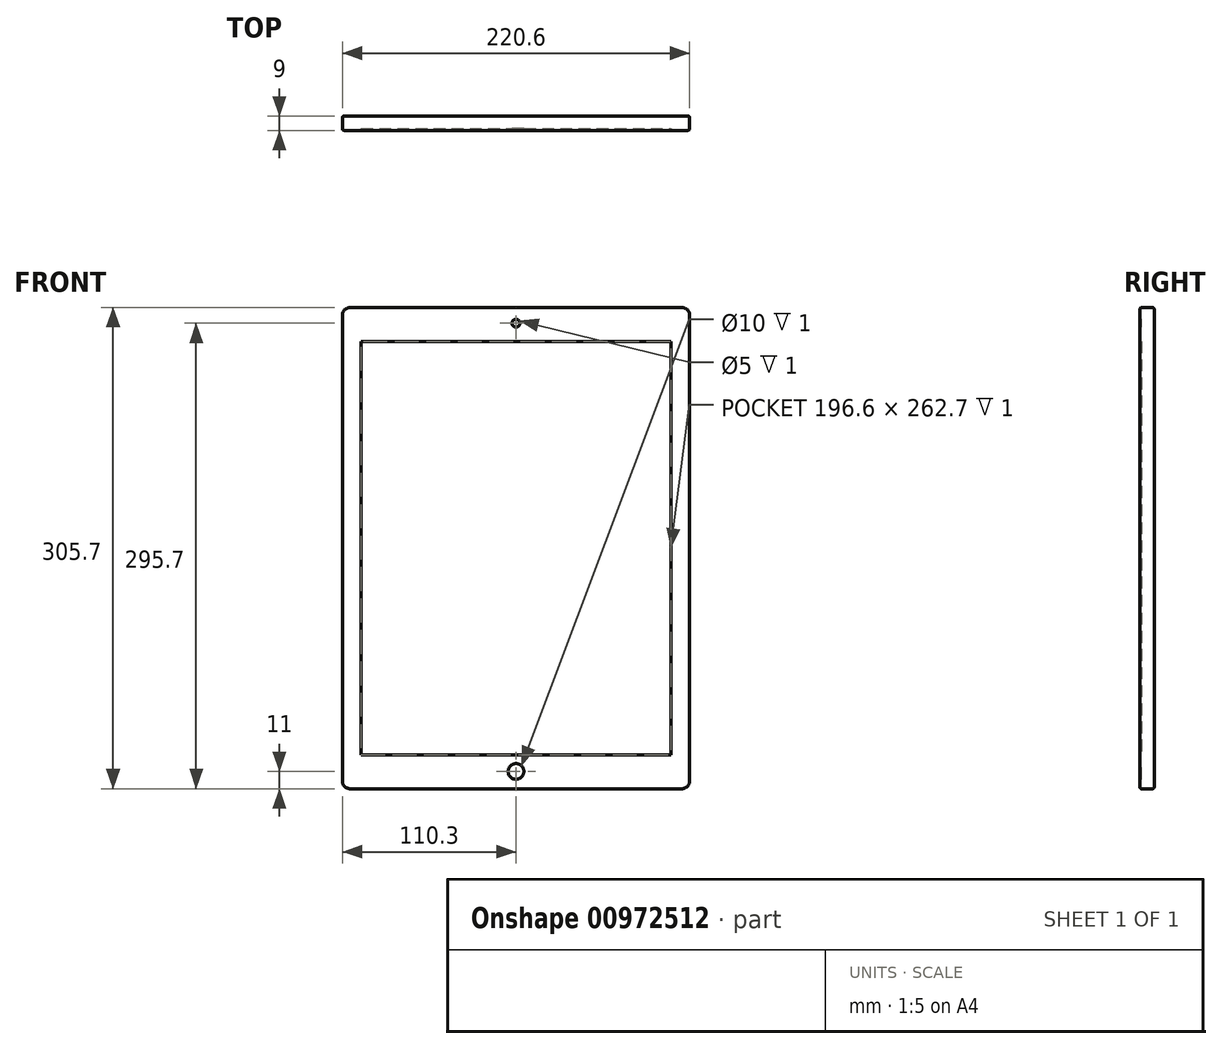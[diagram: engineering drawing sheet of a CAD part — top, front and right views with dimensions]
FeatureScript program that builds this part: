
annotation { "Feature Type Name" : "Feature", "Feature Type Description" : "" }
export const myFeature = defineFeature(function(context is Context, id is Id, definition is map)
    precondition{}
    {
        {
            var Q0;
            Q0=qCreatedBy(makeId("Front.planeOp"),FACE);
            var sketch = newSketch(context, id + "F0", { "sketchPlane" : qUnion([Q0])});
            skLineSegment(sketch, "E0.bottom", {"start": v(-110.3, 305.7) * mm, "end": v(110.3, 305.7) * mm});
            skLineSegment(sketch, "E0.top", {"start": v(-110.3, 0) * mm, "end": v(110.3, 0) * mm});
            skLineSegment(sketch, "E0.left", {"start": v(-110.3, 305.7) * mm, "end": v(-110.3, 0) * mm});
            skLineSegment(sketch, "E0.right", {"start": v(110.3, 305.7) * mm, "end": v(110.3, 0) * mm});
            skSolve(sketch);
        }
        {
            var Q0;
            Q0=makeQuery(id+"F0.imprint","IMPRINT",FACE,{"disambiguationData":[TD([[makeQuery(id+"F0.imprint","IMPRINT",EDGE,{"derivedFrom":sQuery(id+"F0.wireOp",EDGE,"E0.bottom")}),-1.0]])]});
            extrude(context, id + "F1", {"entities" : qUnion([Q0]), "depth" : 9 * mm, "offsetDistance" : 25 * mm});
        }
        {
            var Q0;
            Q0=makeQuery(id+"F1.opExtrude","CAP_FACE",FACE,{"disambiguationData":[OSD([sQuery(id+"F0.wireOp",EDGE,"E0.bottom"),sQuery(id+"F0.wireOp",EDGE,"E0.top"),sQuery(id+"F0.wireOp",EDGE,"E0.left"),sQuery(id+"F0.wireOp",EDGE,"E0.right")])],"isStart":false});
            var sketch = newSketch(context, id + "F2", { "sketchPlane" : qUnion([Q0])});
            skLineSegment(sketch, "E1.bottom", {"start": v(-98.3, 284.2) * mm, "end": v(98.3, 284.2) * mm});
            skLineSegment(sketch, "E1.top", {"start": v(-98.3, 21.5) * mm, "end": v(98.3, 21.5) * mm});
            skLineSegment(sketch, "E1.left", {"start": v(-98.3, 284.2) * mm, "end": v(-98.3, 21.5) * mm});
            skLineSegment(sketch, "E1.right", {"start": v(98.3, 284.2) * mm, "end": v(98.3, 21.5) * mm});
            skLineSegment(sketch, "E2", {"start": v(0, 0) * mm, "end": v(0, 21.5) * mm, "construction": true});
            skLineSegment(sketch, "E3", {"start": v(0, 305.7) * mm, "end": v(0, 284.2) * mm, "construction": true});
            skSolve(sketch);
        }
        {
            var Q0;
            Q0=makeQuery(id+"F2.imprint","IMPRINT",FACE,{"disambiguationData":[TD([[makeQuery(id+"F2.imprint","IMPRINT",EDGE,{"derivedFrom":sQuery(id+"F2.wireOp",EDGE,"E1.bottom")}),-1.0]])]});
            extrude(context, id + "F3", {"entities" : qUnion([Q0]), "operationType" : NewBodyOperationType.REMOVE, "oppositeDirection" : true, "depth" : 1 * mm, "offsetDistance" : 25 * mm});
        }
        {
            var Q0;
            Q0=makeQuery(id+"F1.opExtrude","CAP_FACE",FACE,{"disambiguationData":[OSD([sQuery(id+"F0.wireOp",EDGE,"E0.bottom"),sQuery(id+"F0.wireOp",EDGE,"E0.top"),sQuery(id+"F0.wireOp",EDGE,"E0.left"),sQuery(id+"F0.wireOp",EDGE,"E0.right")])],"isStart":false});
            var sketch = newSketch(context, id + "F4", { "sketchPlane" : qUnion([Q0])});
            skCircle(sketch, "E4", {"center": v(0, 295.7) * mm, "radius": 2.5 * mm});
            skCircle(sketch, "E5", {"center": v(0, 11) * mm, "radius": 5 * mm});
            skLineSegment(sketch, "E6", {"start": v(0, 295.7) * mm, "end": v(0, 11) * mm, "construction": true});
            skLineSegment(sketch, "E7", {"start": v(0, 0) * mm, "end": v(0, 11) * mm, "construction": true});
            skSolve(sketch);
        }
        {
            var Q0;
            Q0=makeQuery(id+"F4.imprint","IMPRINT",FACE,{"disambiguationData":[TD([[makeQuery(id+"F4.imprint","IMPRINT",EDGE,{"derivedFrom":sQuery(id+"F4.wireOp",EDGE,"E4")}),1.0]])]});
            var Q1;
            Q1=makeQuery(id+"F4.imprint","IMPRINT",FACE,{"disambiguationData":[TD([[makeQuery(id+"F4.imprint","IMPRINT",EDGE,{"derivedFrom":sQuery(id+"F4.wireOp",EDGE,"E5")}),1.0]])]});
            extrude(context, id + "F5", {"entities" : qUnion([Q0, Q1]), "operationType" : NewBodyOperationType.REMOVE, "oppositeDirection" : true, "depth" : 1 * mm, "offsetDistance" : 25 * mm});
        }
        {
            var Q0;
            Q0=makeQuery(id+"F1.opExtrude","SWEPT_EDGE",EDGE,{"disambiguationData":[OSD([sQuery(id+"F0.wireOp",EDGE,"E0.top"),sQuery(id+"F0.wireOp",EDGE,"E0.left")])]});
            var Q1;
            Q1=makeQuery(id+"F1.opExtrude","SWEPT_EDGE",EDGE,{"disambiguationData":[OSD([sQuery(id+"F0.wireOp",EDGE,"E0.top"),sQuery(id+"F0.wireOp",EDGE,"E0.right")])]});
            var Q2;
            Q2=makeQuery(id+"F1.opExtrude","SWEPT_EDGE",EDGE,{"disambiguationData":[OSD([sQuery(id+"F0.wireOp",EDGE,"E0.bottom"),sQuery(id+"F0.wireOp",EDGE,"E0.right")])]});
            var Q3;
            Q3=makeQuery(id+"F1.opExtrude","SWEPT_EDGE",EDGE,{"disambiguationData":[OSD([sQuery(id+"F0.wireOp",EDGE,"E0.bottom"),sQuery(id+"F0.wireOp",EDGE,"E0.left")])]});
            fillet(context, id + "F6", {"entities" : qUnion([Q0, Q1, Q2, Q3]), "radius" : 5 * mm, "tangentPropagation" : true, "allowEdgeOverflow" : false});
        }
        {
            var Q0;
            Q0=makeQuery(id+"F1.opExtrude","CAP_EDGE",EDGE,{"disambiguationData":[OSD([sQuery(id+"F0.wireOp",EDGE,"E0.left")])],"isStart":false});
            var Q1;
            Q1=makeQuery(id+"F1.opExtrude","CAP_EDGE",EDGE,{"disambiguationData":[OSD([sQuery(id+"F0.wireOp",EDGE,"E0.left")])],"isStart":true});
            fillet(context, id + "F7", {"entities" : qUnion([Q0, Q1]), "radius" : 1 * mm, "tangentPropagation" : true, "allowEdgeOverflow" : false});
        }
    });
